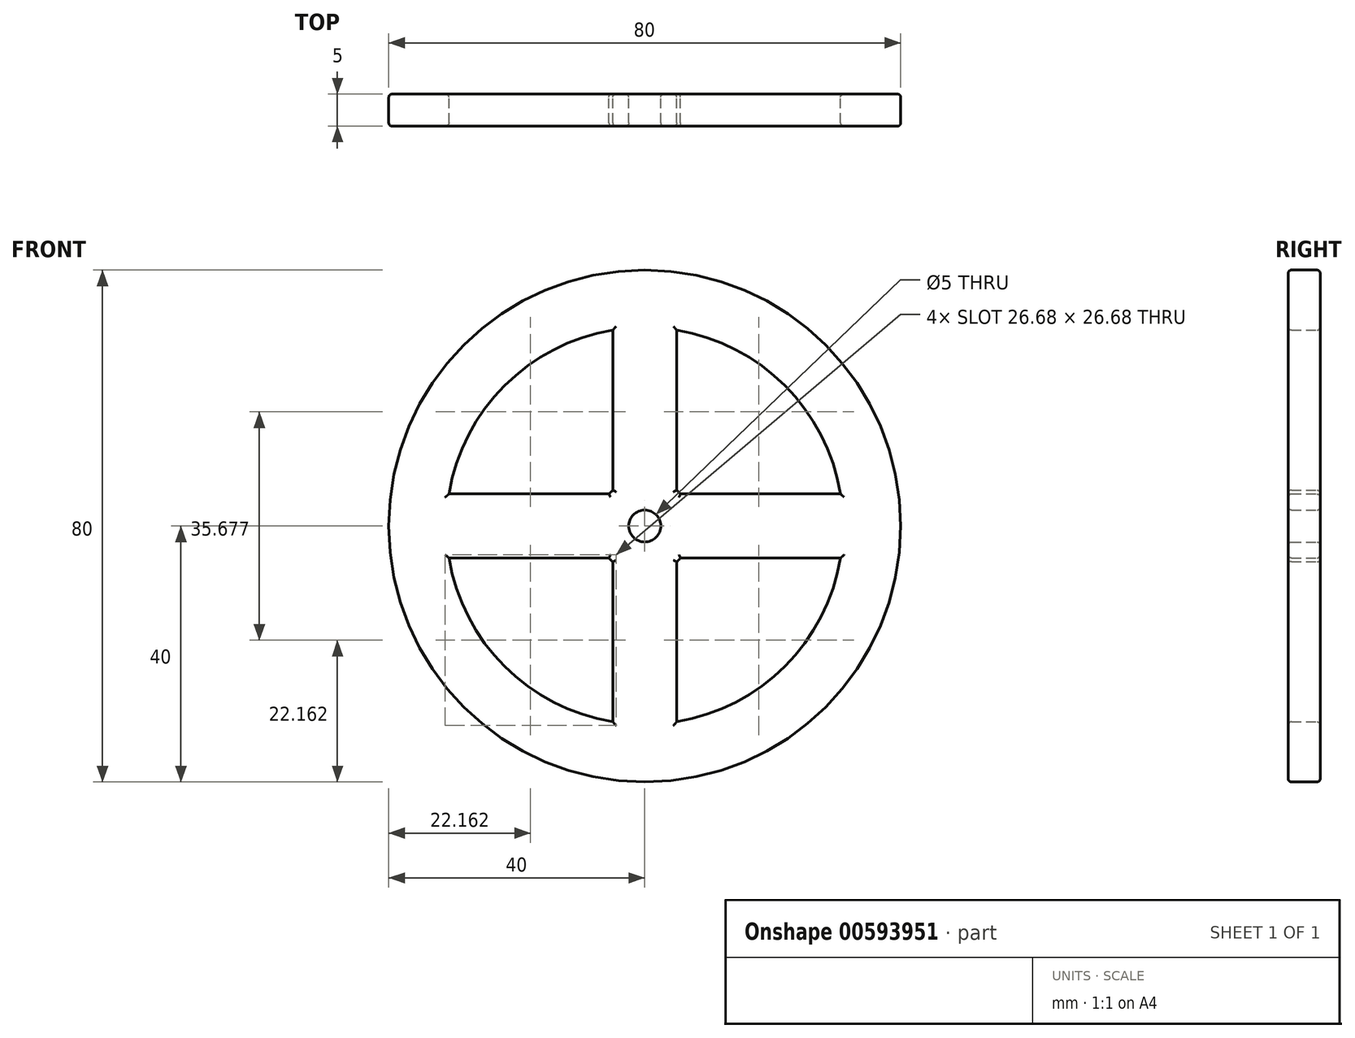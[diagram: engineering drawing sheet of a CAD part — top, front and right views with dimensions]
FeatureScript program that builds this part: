
annotation { "Feature Type Name" : "Feature", "Feature Type Description" : "" }
export const myFeature = defineFeature(function(context is Context, id is Id, definition is map)
    precondition{}
    {
        {
            var Q0;
            Q0=qCreatedBy(makeId("Front.planeOp"),FACE);
            var sketch = newSketch(context, id + "F0", { "sketchPlane" : qUnion([Q0])});
            skCircle(sketch, "E0", {"center": v(0, 0) * mm, "radius": 40 * mm});
            skArc(sketch, "E1", {"start": v(-30.6, -5) * mm, "mid": v(-21.92, -21.92) * mm, "end": v(-5, -30.6) * mm});
            skArc(sketch, "E2", {"start": v(-5.6, -5) * mm, "mid": v(-5.3, -5.3) * mm, "end": v(-5, -5.6) * mm});
            skCircle(sketch, "E3", {"center": v(0, 0) * mm, "radius": 2.5 * mm});
            skLineSegment(sketch, "E4", {"start": v(0, 0) * mm, "end": v(0, 31) * mm});
            skLineSegment(sketch, "E5", {"start": v(0, 0) * mm, "end": v(0, -31) * mm});
            skLineSegment(sketch, "E6", {"start": v(0, 0) * mm, "end": v(-31, 0) * mm});
            skLineSegment(sketch, "E7", {"start": v(0, 0) * mm, "end": v(31, 0) * mm});
            skLineSegment(sketch, "E8.0", {"start": v(-5, 5.6) * mm, "end": v(-5, 30.6) * mm});
            skLineSegment(sketch, "E9.0", {"start": v(5, 5.6) * mm, "end": v(5, 30.6) * mm});
            skLineSegment(sketch, "E10.0", {"start": v(-5.6, 5) * mm, "end": v(-30.6, 5) * mm});
            skLineSegment(sketch, "E11.0", {"start": v(-5.6, -5) * mm, "end": v(-30.6, -5) * mm});
            skLineSegment(sketch, "E12.0", {"start": v(-5, -5.6) * mm, "end": v(-5, -30.6) * mm});
            skLineSegment(sketch, "E13.0", {"start": v(5, -5.6) * mm, "end": v(5, -30.6) * mm});
            skLineSegment(sketch, "E14.0", {"start": v(5.6, -5) * mm, "end": v(30.6, -5) * mm});
            skLineSegment(sketch, "E15.0", {"start": v(5.6, 5) * mm, "end": v(30.6, 5) * mm});
            skArc(sketch, "E16.trimOffspring", {"start": v(5, -5.6) * mm, "mid": v(5.3, -5.3) * mm, "end": v(5.6, -5) * mm});
            skArc(sketch, "E17.trimOffspring", {"start": v(-5, 5.6) * mm, "mid": v(-5.3, 5.3) * mm, "end": v(-5.6, 5) * mm});
            skArc(sketch, "E18.trimOffspring", {"start": v(5.6, 5) * mm, "mid": v(5.3, 5.3) * mm, "end": v(5, 5.6) * mm});
            skArc(sketch, "E19.trimOffspring", {"start": v(5, -30.6) * mm, "mid": v(21.92, -21.92) * mm, "end": v(30.6, -5) * mm});
            skArc(sketch, "E20.trimOffspring", {"start": v(30.6, 5) * mm, "mid": v(21.92, 21.92) * mm, "end": v(5, 30.6) * mm});
            skArc(sketch, "E21.trimOffspring", {"start": v(-5, 30.6) * mm, "mid": v(-21.92, 21.92) * mm, "end": v(-30.6, 5) * mm});
            skSolve(sketch);
        }
        {
            var Q0;
            Q0=makeQuery(id+"F0.imprint","IMPRINT",FACE,{"disambiguationData":[TD([[makeQuery(id+"F0.imprint","IMPRINT",EDGE,{"derivedFrom":sQuery(id+"F0.wireOp",EDGE,"E0")}),1.0]])]});
            extrude(context, id + "F1", {"entities" : qUnion([Q0]), "endBound" : BoundingType.SYMMETRIC, "depth" : 5 * mm, "offsetDistance" : 25 * mm});
        }
        {
            var Q0;
            Q0=makeQuery(id+"F1.opExtrude","CAP_FACE",FACE,{"disambiguationData":[OSD([sQuery(id+"F0.wireOp",EDGE,"E0"),sQuery(id+"F0.wireOp",EDGE,"E1"),sQuery(id+"F0.wireOp",EDGE,"E2"),sQuery(id+"F0.wireOp",EDGE,"E3"),sQuery(id+"F0.wireOp",EDGE,"E8.0"),sQuery(id+"F0.wireOp",EDGE,"E9.0"),sQuery(id+"F0.wireOp",EDGE,"E10.0"),sQuery(id+"F0.wireOp",EDGE,"E11.0"),sQuery(id+"F0.wireOp",EDGE,"E12.0"),sQuery(id+"F0.wireOp",EDGE,"E13.0"),sQuery(id+"F0.wireOp",EDGE,"E14.0"),sQuery(id+"F0.wireOp",EDGE,"E15.0"),sQuery(id+"F0.wireOp",EDGE,"E16.trimOffspring"),sQuery(id+"F0.wireOp",EDGE,"E17.trimOffspring"),sQuery(id+"F0.wireOp",EDGE,"E18.trimOffspring"),sQuery(id+"F0.wireOp",EDGE,"E19.trimOffspring"),sQuery(id+"F0.wireOp",EDGE,"E20.trimOffspring"),sQuery(id+"F0.wireOp",EDGE,"E21.trimOffspring")])],"isStart":true});
            var Q1;
            Q1=makeQuery(id+"F1.opExtrude","CAP_FACE",FACE,{"disambiguationData":[OSD([sQuery(id+"F0.wireOp",EDGE,"E0"),sQuery(id+"F0.wireOp",EDGE,"E1"),sQuery(id+"F0.wireOp",EDGE,"E2"),sQuery(id+"F0.wireOp",EDGE,"E3"),sQuery(id+"F0.wireOp",EDGE,"E8.0"),sQuery(id+"F0.wireOp",EDGE,"E9.0"),sQuery(id+"F0.wireOp",EDGE,"E10.0"),sQuery(id+"F0.wireOp",EDGE,"E11.0"),sQuery(id+"F0.wireOp",EDGE,"E12.0"),sQuery(id+"F0.wireOp",EDGE,"E13.0"),sQuery(id+"F0.wireOp",EDGE,"E14.0"),sQuery(id+"F0.wireOp",EDGE,"E15.0"),sQuery(id+"F0.wireOp",EDGE,"E16.trimOffspring"),sQuery(id+"F0.wireOp",EDGE,"E17.trimOffspring"),sQuery(id+"F0.wireOp",EDGE,"E18.trimOffspring"),sQuery(id+"F0.wireOp",EDGE,"E19.trimOffspring"),sQuery(id+"F0.wireOp",EDGE,"E20.trimOffspring"),sQuery(id+"F0.wireOp",EDGE,"E21.trimOffspring")])],"isStart":false});
            fillet(context, id + "F2", {"entities" : qUnion([Q0, Q1]), "radius" : 0.5 * mm, "tangentPropagation" : true, "allowEdgeOverflow" : false});
        }
    });
